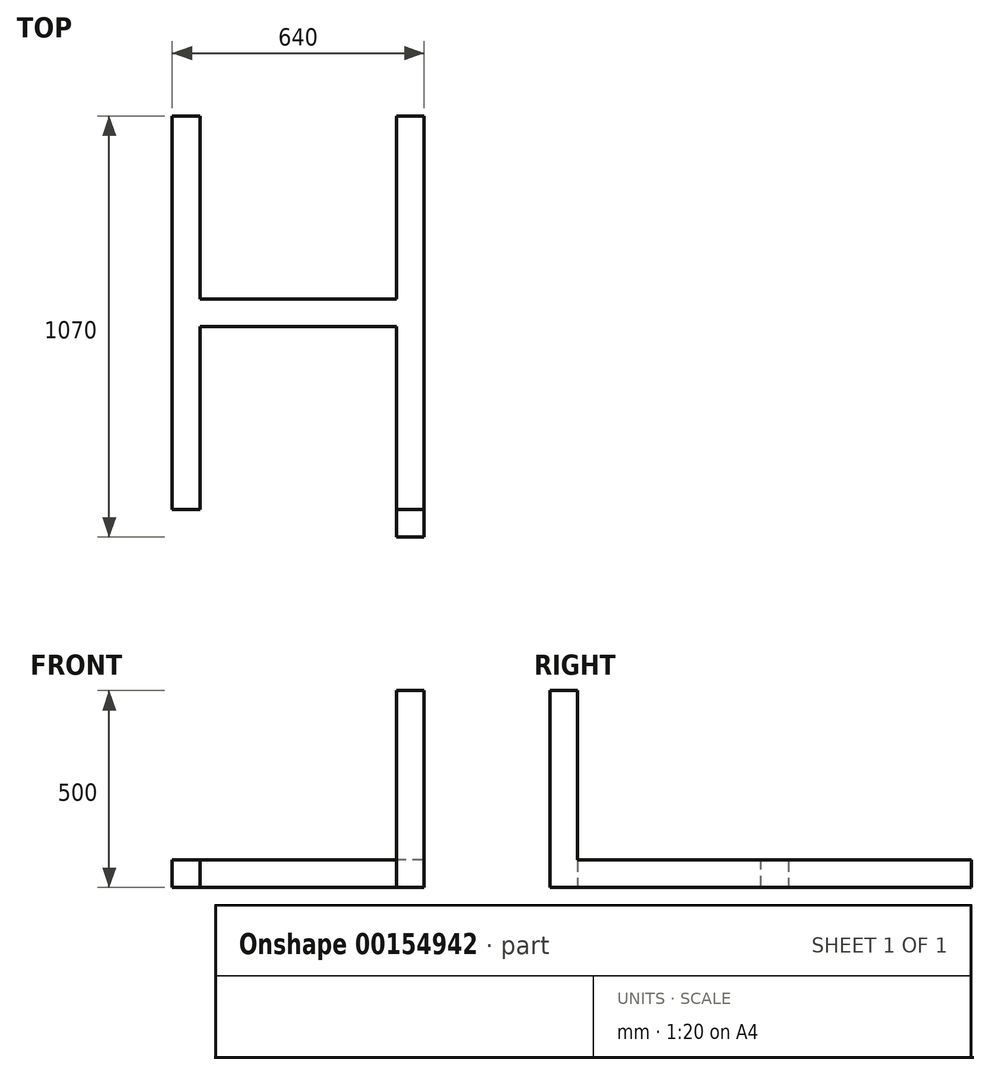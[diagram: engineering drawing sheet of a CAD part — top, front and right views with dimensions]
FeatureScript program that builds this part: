
annotation { "Feature Type Name" : "Feature", "Feature Type Description" : "" }
export const myFeature = defineFeature(function(context is Context, id is Id, definition is map)
    precondition{}
    {
        {
            var Q0;
            Q0=qCreatedBy(makeId("Front.planeOp"),FACE);
            var sketch = newSketch(context, id + "F0", { "sketchPlane" : qUnion([Q0])});
            skLineSegment(sketch, "E0.bottom", {"start": v(35, 35) * mm, "end": v(-35, 35) * mm});
            skLineSegment(sketch, "E0.top", {"start": v(35, -35) * mm, "end": v(-35, -35) * mm});
            skLineSegment(sketch, "E0.left", {"start": v(35, 35) * mm, "end": v(35, -35) * mm});
            skLineSegment(sketch, "E0.right", {"start": v(-35, 35) * mm, "end": v(-35, -35) * mm});
            skPoint(sketch, "E0.middle", {"position": v(0, 0) * mm});
            skSolve(sketch);
        }
        {
            var Q0;
            Q0=makeQuery(id+"F0.imprint","IMPRINT",FACE,{"disambiguationData":[TD([[makeQuery(id+"F0.imprint","IMPRINT",EDGE,{"derivedFrom":sQuery(id+"F0.wireOp",EDGE,"E0.bottom")}),1.0]])]});
            extrude(context, id + "F1", {"entities" : qUnion([Q0]), "depth" : 1000 * mm});
        }
        {
            var Q0;
            Q0=makeQuery(id+"F1.opExtrude","SWEPT_FACE",FACE,{"disambiguationData":[OSD([sQuery(id+"F0.wireOp",EDGE,"E0.left")])]});
            var sketch = newSketch(context, id + "F2", { "sketchPlane" : qUnion([Q0])});
            skLineSegment(sketch, "E1", {"start": v(-500, 35) * mm, "end": v(-465, 35) * mm});
            skLineSegment(sketch, "E2", {"start": v(-465, 35) * mm, "end": v(-465, -35) * mm});
            skLineSegment(sketch, "E3", {"start": v(-465, -35) * mm, "end": v(-535, -35) * mm});
            skLineSegment(sketch, "E4", {"start": v(-535, -35) * mm, "end": v(-535, 35) * mm});
            skLineSegment(sketch, "E5", {"start": v(-535, 35) * mm, "end": v(-500, 35) * mm});
            skSolve(sketch);
        }
        {
            var Q0;
            Q0=makeQuery(id+"F2.imprint","IMPRINT",FACE,{"disambiguationData":[TD([[makeQuery(id+"F2.imprint","IMPRINT",EDGE,{"derivedFrom":sQuery(id+"F2.wireOp",EDGE,"E1")}),-1.0]])]});
            extrude(context, id + "F3", {"entities" : qUnion([Q0]), "operationType" : NewBodyOperationType.ADD, "depth" : 500 * mm});
        }
        {
            var Q0;
            Q0=makeQuery(id+"F3.opExtrude","SWEPT_FACE",FACE,{"disambiguationData":[OSD([sQuery(id+"F2.wireOp",EDGE,"E4")])]});
            var sketch = newSketch(context, id + "F4", { "sketchPlane" : qUnion([Q0])});
            skLineSegment(sketch, "E6", {"start": v(535, 35) * mm, "end": v(605, 35) * mm});
            skLineSegment(sketch, "E7", {"start": v(605, 35) * mm, "end": v(605, -35) * mm});
            skLineSegment(sketch, "E8", {"start": v(605, -35) * mm, "end": v(535, -35) * mm});
            skLineSegment(sketch, "E9", {"start": v(535, -35) * mm, "end": v(535, 35) * mm});
            skSolve(sketch);
        }
        {
            var Q0;
            Q0=makeQuery(id+"F4.imprint","IMPRINT",FACE,{"disambiguationData":[TD([[makeQuery(id+"F4.imprint","IMPRINT",EDGE,{"derivedFrom":sQuery(id+"F4.wireOp",EDGE,"E6")}),-1.0]])]});
            extrude(context, id + "F5", {"entities" : qUnion([Q0]), "operationType" : NewBodyOperationType.ADD, "oppositeDirection" : true, "depth" : 535 * mm});
        }
        {
            var Q0;
            Q0=makeQuery(id+"F5.boolean.opBoolean","MERGE",FACE,{"derivedFrom":[makeQuery(id+"F3.opExtrude","SWEPT_FACE",FACE,{"disambiguationData":[OSD([sQuery(id+"F2.wireOp",EDGE,"E4")])]}),makeQuery(id+"F5.opExtrude","CAP_FACE",FACE,{"disambiguationData":[OSD([sQuery(id+"F4.wireOp",EDGE,"E6"),sQuery(id+"F4.wireOp",EDGE,"E7"),sQuery(id+"F4.wireOp",EDGE,"E8"),sQuery(id+"F4.wireOp",EDGE,"E9")])],"isStart":true})]});
            var sketch = newSketch(context, id + "F6", { "sketchPlane" : qUnion([Q0])});
            skLineSegment(sketch, "E10.bottom", {"start": v(605, 35) * mm, "end": v(535, 35) * mm});
            skLineSegment(sketch, "E10.top", {"start": v(605, -35) * mm, "end": v(535, -35) * mm});
            skLineSegment(sketch, "E10.left", {"start": v(605, 35) * mm, "end": v(605, -35) * mm});
            skLineSegment(sketch, "E10.right", {"start": v(535, 35) * mm, "end": v(535, -35) * mm});
            skSolve(sketch);
        }
        {
            var Q0;
            Q0=makeQuery(id+"F6.imprint","IMPRINT",FACE,{"disambiguationData":[TD([[makeQuery(id+"F6.imprint","IMPRINT",EDGE,{"derivedFrom":sQuery(id+"F6.wireOp",EDGE,"E10.bottom")}),1.0]])]});
            extrude(context, id + "F7", {"entities" : qUnion([Q0]), "operationType" : NewBodyOperationType.ADD, "depth" : 465 * mm});
        }
        {
            var Q0;
            Q0=makeQuery(id+"F7.boolean.opBoolean","MERGE",FACE,{"derivedFrom":[makeQuery(id+"F5.boolean.opBoolean","MERGE",FACE,{"derivedFrom":[makeQuery(id+"F3.boolean.opBoolean","MERGE",FACE,{"derivedFrom":[makeQuery(id+"F1.opExtrude","SWEPT_FACE",FACE,{"disambiguationData":[OSD([sQuery(id+"F0.wireOp",EDGE,"E0.top")])]}),makeQuery(id+"F3.opExtrude","SWEPT_FACE",FACE,{"disambiguationData":[OSD([sQuery(id+"F2.wireOp",EDGE,"E3")])]})]}),makeQuery(id+"F5.opExtrude","SWEPT_FACE",FACE,{"disambiguationData":[OSD([sQuery(id+"F4.wireOp",EDGE,"E8")])]})]}),makeQuery(id+"F7.opExtrude","SWEPT_FACE",FACE,{"disambiguationData":[OSD([sQuery(id+"F6.wireOp",EDGE,"E10.top")])]})]});
            var sketch = newSketch(context, id + "F8", { "sketchPlane" : qUnion([Q0])});
            skLineSegment(sketch, "E11", {"start": v(535, 1000) * mm, "end": v(535, 1070) * mm});
            skLineSegment(sketch, "E12", {"start": v(535, 1070) * mm, "end": v(605, 1070) * mm});
            skLineSegment(sketch, "E13", {"start": v(605, 1070) * mm, "end": v(605, 1000) * mm});
            skLineSegment(sketch, "E14", {"start": v(605, 1000) * mm, "end": v(535, 1000) * mm});
            skSolve(sketch);
        }
        {
            var Q0;
            Q0=makeQuery(id+"F8.imprint","IMPRINT",FACE,{"disambiguationData":[TD([[makeQuery(id+"F8.imprint","IMPRINT",EDGE,{"derivedFrom":sQuery(id+"F8.wireOp",EDGE,"E11")}),-1.0]])]});
            extrude(context, id + "F9", {"entities" : qUnion([Q0]), "operationType" : NewBodyOperationType.ADD, "oppositeDirection" : true, "depth" : 500 * mm});
        }
    });
